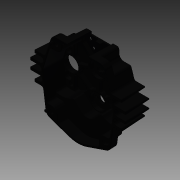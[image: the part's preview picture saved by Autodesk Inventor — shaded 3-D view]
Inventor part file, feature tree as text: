
AUTODESK INVENTOR PART (.ipt)
format: ipt  version: 2013 (Build 170138000, 138)  size: 3,690,496 bytes
history: native  units: in
note: dims shown in document units (in); Inventor stores cm internally (conversion verified against a paired STEP export)
features: projected_geometry x4, sketch x3, other x2, extrude x2, hole x1, imported_body x1
ambient origin geometry x8: Origin, YZ Plane, XZ Plane, XY Plane, X Axis, Y Axis, Z Axis, Center Point
feature tree (13):
  other  "Toughbox-mini_d01-5-12"
  other  "Toughbox-mini_d01-5-121"
  extrude  "Extrusion1"  Depth=1.25in
  hole  "Hole1"  [1 undecoded]
  extrude  "Extrusion2"  Depth=0.1875in
  imported_body  "Base1"
  sketch  "Sketch1"  dims[d0=1.125in d2=1.25in]
  sketch  "Sketch2"  dims[d3=0.3937in d4=0.0in d5=0.0787in]
  projected_geometry  "Projected Loop1"
  projected_geometry  "Projected Loop2"
  projected_geometry  "Projected Loop3"
  projected_geometry  "Projected Loop4"
  sketch  "Sketch3"  dims[d6=0.875in d9=0.1875in d10=0.75in d11=0.1875in d12=0.2362in d13=0.1575in d14=0.0787in d15=90.0deg d16=0.315in d17=0.8108in d18=0.375in d19=1.25in d22=0.3937in d23=0.0in d24=1.25in d26=0.0394in d27=0.0787in]
note: 1 required parameter value undecoded (feature->parameter linkage not recoverable at this tier; creation-order binding heuristic only, values carry confidence <= 0.55)
